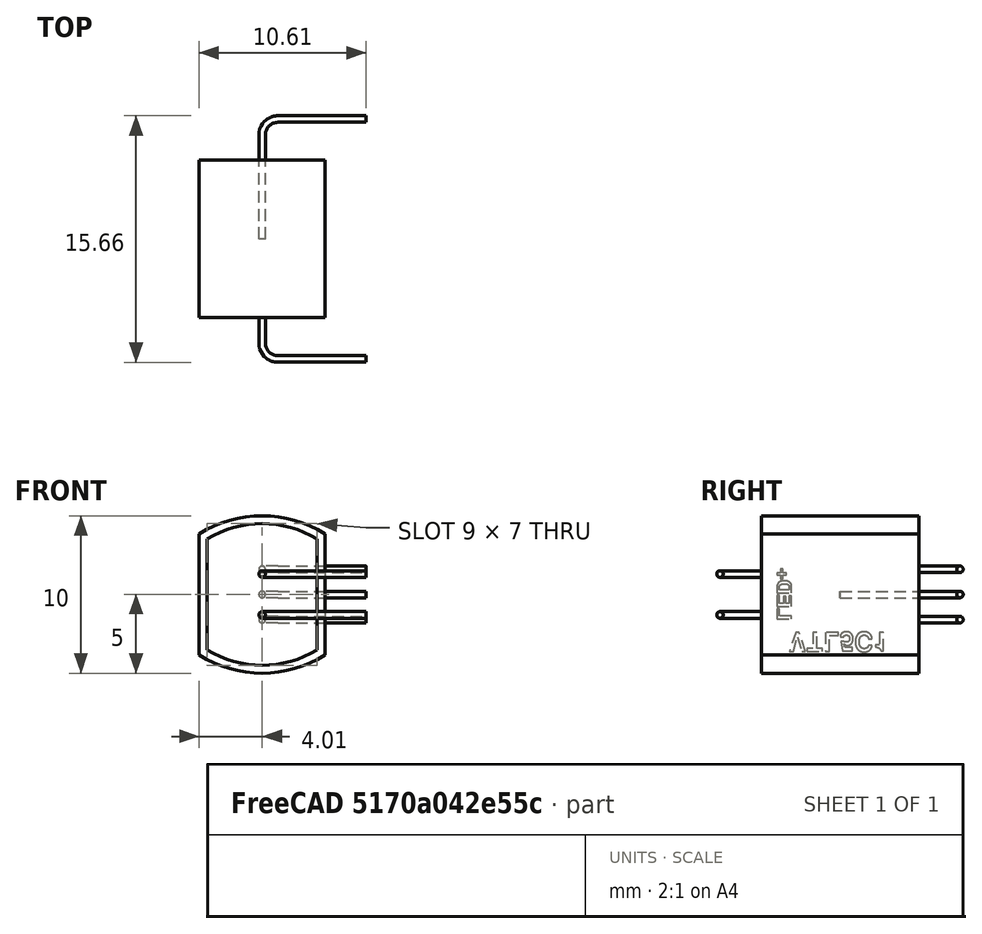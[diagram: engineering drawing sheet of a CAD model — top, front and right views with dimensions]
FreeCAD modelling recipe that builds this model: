
FCSTD DOCUMENT  (FreeCAD 0.19R16945 (Git))
Label: Xvive_VTL5C1
License: All rights reserved
LicenseURL: http://en.wikipedia.org/wiki/All_rights_reserved
objects: PartDesign::Body×7, PartDesign::FeatureBase×5, Sketcher::SketchObject×4, Part::Part2DObjectPython×2, Part::Extrusion×2, PartDesign::Pad×1, PartDesign::Pocket×1, PartDesign::Mirrored×1, PartDesign::AdditivePipe×1, Spreadsheet::Sheet×1, Part::MultiFuse×1
note: 28 computed .brp shape members not serialized (recipe doc carries the construction recipe); baked Part::Feature solids carry a one-line shape summary decoded from their .brp

FEATURE [Sketcher::SketchObject] Sketch
  MapMode = 5
  Placement = pos=(0,0,0) rot=(1,0,0;1.5708rad)
  Support = -> [XZ_Plane]
  expr: Constraints[12] = Spreadsheet.bodyheight
  expr: Constraints[13] = Spreadsheet.bodylength
  sketch-geometry (6):
    g0: LineSegment StartX=-4 StartY=3.84429 StartZ=0 EndX=-4 EndY=-3.84429 EndZ=0
    g1: LineSegment StartX=4 StartY=3.84429 StartZ=0 EndX=4 EndY=-3.84429 EndZ=0
    g2: ArcOfCircle CenterX=0 CenterY=-2.5 CenterZ=0 NormalX=0 NormalY=0 NormalZ=1 AngleXU=0 Radius=7.5 StartAngle=1.00826 EndAngle=2.13333
    g3: ArcOfCircle CenterX=0 CenterY=2.5 CenterZ=0 NormalX=0 NormalY=0 NormalZ=1 AngleXU=0 Radius=7.5 StartAngle=4.14985 EndAngle=5.27493
    g4: GeomPoint X=0 Y=5 Z=0
    g5: GeomPoint X=0 Y=-5 Z=0
  constraints (16):
    c: Vertical(g1)
    c: PointOnObject(g2,g-2)
    c: Coincident(g2,g0)
    c: Coincident(g2,g1)
    c: PointOnObject(g3,g-2)
    c: Coincident(g3,g0)
    c: Coincident(g3,g1)
    c: PointOnObject(g4,g2)
    c: PointOnObject(g5,g3)
    c: PointOnObject(g4,g-2)
    c: Symmetric(g0,g0,g-1)
    c: Equal(g2,g3)
    c: DistanceX(g0,g1) = 8
    c: DistanceY(g5,g4) = 10
    c: Equal(g1,g0)
    c: Symmetric(g5,g-1,g2)
FEATURE [PartDesign::Pad] Pad
  Length = 10
  Length2 = 100
  Midplane = true
  Placement = pos=(0,0,0) rot=(1,0,0;1.5708rad)
  Profile = -> Sketch
  Type = 0
FEATURE [Sketcher::SketchObject] Sketch001
  MapMode = 5
  Placement = pos=(0,-5,0) rot=(1,0,0;1.5708rad)
  Support = -> [Pad]
  expr: Constraints[13] = Sketch.Constraints[13] - 1mm
  expr: Constraints[12] = Sketch.Constraints[12] - 1mm
  sketch-geometry (6):
    g0: LineSegment StartX=-3.5 StartY=3.5217 StartZ=0 EndX=-3.5 EndY=-3.5217 EndZ=0
    g1: LineSegment StartX=3.5 StartY=3.5217 StartZ=0 EndX=3.5 EndY=-3.5217 EndZ=0
    g2: ArcOfCircle CenterX=0 CenterY=-2.25 CenterZ=0 NormalX=0 NormalY=0 NormalZ=1 AngleXU=0 Radius=6.75 StartAngle=1.02568 EndAngle=2.11591
    g3: ArcOfCircle CenterX=0 CenterY=2.25 CenterZ=0 NormalX=0 NormalY=0 NormalZ=1 AngleXU=0 Radius=6.75 StartAngle=4.16727 EndAngle=5.25751
    g4: GeomPoint X=0 Y=4.5 Z=0
    g5: GeomPoint X=0 Y=-4.5 Z=0
  constraints (16):
    c: Vertical(g1)
    c: PointOnObject(g2,g-2)
    c: Coincident(g2,g0)
    c: Coincident(g2,g1)
    c: PointOnObject(g3,g-2)
    c: Coincident(g3,g0)
    c: Coincident(g3,g1)
    c: PointOnObject(g4,g2)
    c: PointOnObject(g5,g3)
    c: PointOnObject(g4,g-2)
    c: Symmetric(g0,g0,g-1)
    c: Equal(g2,g3)
    c: DistanceX(g0,g1) = 7
    c: DistanceY(g5,g4) = 9
    c: Equal(g1,g0)
    c: Symmetric(g5,g-1,g2)
FEATURE [PartDesign::Pocket] Pocket
  BaseFeature = -> Pad
  Length = 0.01
  Length2 = 100
  Placement = pos=(0,0,0) rot=(1,0,0;1.5708rad)
  Profile = -> Sketch001
  Type = 0
FEATURE [PartDesign::Mirrored] Mirrored
  BaseFeature = -> Pocket
  MirrorPlane = -> XZ_Plane
  Originals = -> [Pocket]
  Placement = pos=(0,0,0) rot=(1,0,0;1.5708rad)
FEATURE [PartDesign::Body] Body
  Group = -> [Sketch,Pad,Sketch001,Pocket,Mirrored]
  Origin = -> Origin
  Tip = -> Mirrored
FEATURE [Sketcher::SketchObject] Sketch004  label="LeadDiameter"
  AttachmentOffset = pos=(0,0,4) rot=(0,0,1;0rad)
  MapMode = 5
  Placement = pos=(0,-4,-9e-16) rot=(1,0,0;1.5708rad)
  Support = -> [XZ_Plane002]
  expr: AttachmentOffset.Base.z = Spreadsheet.bodylength / 2 - 1mm
  expr: AttachmentOffset.Base.y = 0
  expr: Constraints[1] = Spreadsheet.leaddialed / 2
  sketch-geometry (1):
    g0: Circle CenterX=0 CenterY=0 CenterZ=0 NormalX=0 NormalY=0 NormalZ=1 AngleXU=0 Radius=0.2075
  constraints (2):
    c: Coincident(g0,g-1)
    c: Radius(g0) = 0.2075
FEATURE [Sketcher::SketchObject] Sketch005  label="LeadProfile"
  MapMode = 5
  Support = -> [XY_Plane002]
  expr: Constraints[6] = Spreadsheet.leadpitch / 2
  expr: Constraints[7] = Spreadsheet.bodyheight / 2 + Spreadsheet.leadextralength
  sketch-geometry (3):
    g0: LineSegment StartX=0 StartY=0 StartZ=0 EndX=0 EndY=-6.62 EndZ=0
    g1: LineSegment StartX=1 StartY=-7.62 StartZ=0 EndX=6.6 EndY=-7.62 EndZ=0
    g2: ArcOfCircle CenterX=1 CenterY=-6.62 CenterZ=0 NormalX=0 NormalY=0 NormalZ=1 AngleXU=0 Radius=1 StartAngle=3.14159 EndAngle=4.71239
  constraints (8):
    c: Coincident(g0,g-1)
    c: Horizontal(g1)
    c: Tangent(g0,g2) = -1.5708
    c: Tangent(g1,g2) = -1.5708
    c: Radius(g2) = 1
    c: PointOnObject(g0,g-2)
    c: DistanceY(g1,g0) = 7.62
    c: DistanceX(g0,g1) = 6.6
FEATURE [PartDesign::AdditivePipe] AdditivePipe
  AuxilleryCurvelinear = true
  AuxillerySpineTangent = false
  Binormal = (0,0,0)
  Mode = 0
  Placement = pos=(0,0,0) rot=(1,0,0;1.5708rad)
  Profile = -> Sketch004
  Spine = -> Sketch005
  SpineTangent = false
  Transformation = 0
  Transition = 0
FEATURE [PartDesign::Body] Body002  label="Lead"
  Group = -> [Sketch004,Sketch005,AdditivePipe]
  Origin = -> Origin002
  Tip = -> AdditivePipe
FEATURE [Spreadsheet::Sheet] Spreadsheet
  cells = A2=bodylength; B2(bodylength)==10mm; A3=bodyheight; B3(bodyheight)==8mm; A4=pottingmaxheight; B4(pottingmaxheight)==2.5mm; A6=leaddialed; B6(leaddialed)==0.415mm; A7=leadpitchled; B7(leadpitchled)==2.6mm; A8=leadpitchldr; B8(leadpitchldr)==3.2mm; A10=leadpitch; B10(leadpitch)==6 * 2.54mm; A11=leadextralength; B11(leadextralength)==2.6mm
FEATURE [Part::Part2DObjectPython] ShapeString  # Draft 2D object (typed FeaturePython)
  AttachmentOffset = pos=(5.5,-1,0) rot=(0,0,1;3.14159rad)
  FontFile = <userpath>/Desktop/GitHub/freecad-projects/00-fonts/FreeSansBold.ttf
  MapMode = 6
  Placement = pos=(-4,-4,-1.65571) rot=(0,-1,0;1.5708rad)
  Size = 0.5
  String = LED+
  Support = -> [Mirrored]
  Tracking = 0
FEATURE [Part::Extrusion] Extrude  label="MarkingLED"
  Base = -> ShapeString
  Dir = (-1,0,-2e-16)
  DirMode = 2
  FaceMakerClass = Part::FaceMakerBullseye
  LengthFwd = 0.01
  LengthRev = 0
  Solid = false
  Symmetric = false
FEATURE [Part::Part2DObjectPython] ShapeString001  # Draft 2D object (typed FeaturePython)
  AttachmentOffset = pos=(6.25,-1.75,0) rot=(0,0,1;-1.5708rad)
  FontFile = <userpath>/Desktop/GitHub/freecad-projects/00-fonts/FreeSansBold.ttf
  MapMode = 6
  Placement = pos=(-4,-3.25,-2.40571) rot=(-0.57735,-0.57735,0.57735;2.0944rad)
  Size = 0.65
  String = VTL5C1
  Support = -> [Mirrored]
  Tracking = 0
FEATURE [Part::Extrusion] Extrude001  label="MarkingVTL"
  Base = -> ShapeString001
  Dir = (-1,0,-2e-16)
  DirMode = 2
  FaceMakerClass = Part::FaceMakerBullseye
  LengthFwd = 0.01
  LengthRev = 0
  Solid = false
  Symmetric = false
FEATURE [PartDesign::FeatureBase] Clone
  BaseFeature = -> Body002
FEATURE [PartDesign::Body] Body003  label="LeadCloneLED1"
  BaseFeature = -> Body002
  Group = -> [Clone]
  Origin = -> Origin003
  Placement = pos=(0,0,1.3) rot=(0,0,1;0rad)
  Tip = -> Clone
  expr: Placement.Base.z = Spreadsheet.leadpitchled / 2
FEATURE [PartDesign::FeatureBase] Clone001
  BaseFeature = -> Body002
FEATURE [PartDesign::Body] Body004  label="LeadCloneLED2"
  BaseFeature = -> Body002
  Group = -> [Clone001]
  Origin = -> Origin004
  Placement = pos=(0,0,-1.3) rot=(0,0,1;0rad)
  Tip = -> Clone001
  expr: Placement.Base.z = -Spreadsheet.leadpitchled / 2
FEATURE [PartDesign::FeatureBase] Clone002
  BaseFeature = -> Body002
FEATURE [PartDesign::Body] Body005  label="LeadCloneLDR1"
  BaseFeature = -> Body002
  Group = -> [Clone002]
  Origin = -> Origin005
  Placement = pos=(0,0,1.6) rot=(1,0,0;3.14159rad)
  Tip = -> Clone002
  expr: Placement.Base.z = Spreadsheet.leadpitchldr / 2
FEATURE [PartDesign::FeatureBase] Clone003
  BaseFeature = -> Body002
FEATURE [PartDesign::Body] Body006  label="LeadCloneLDR2"
  BaseFeature = -> Body002
  Group = -> [Clone003]
  Origin = -> Origin006
  Placement = pos=(0,0,-1.6) rot=(1,0,0;3.14159rad)
  Tip = -> Clone003
  expr: Placement.Base.z = -Spreadsheet.leadpitchldr / 2
FEATURE [PartDesign::FeatureBase] Clone004
  BaseFeature = -> Body002
FEATURE [PartDesign::Body] Body007  label="LeadCloneLDR3"
  BaseFeature = -> Body002
  Group = -> [Clone004]
  Origin = -> Origin007
  Placement = pos=(0,0,0) rot=(1,0,0;3.14159rad)
  Tip = -> Clone004
FEATURE [Part::MultiFuse] Fusion  label="Xvive_VTL5C1"
  Shapes = -> [Body006,Body003,Extrude,Extrude001,Body005,Body004,Body]
